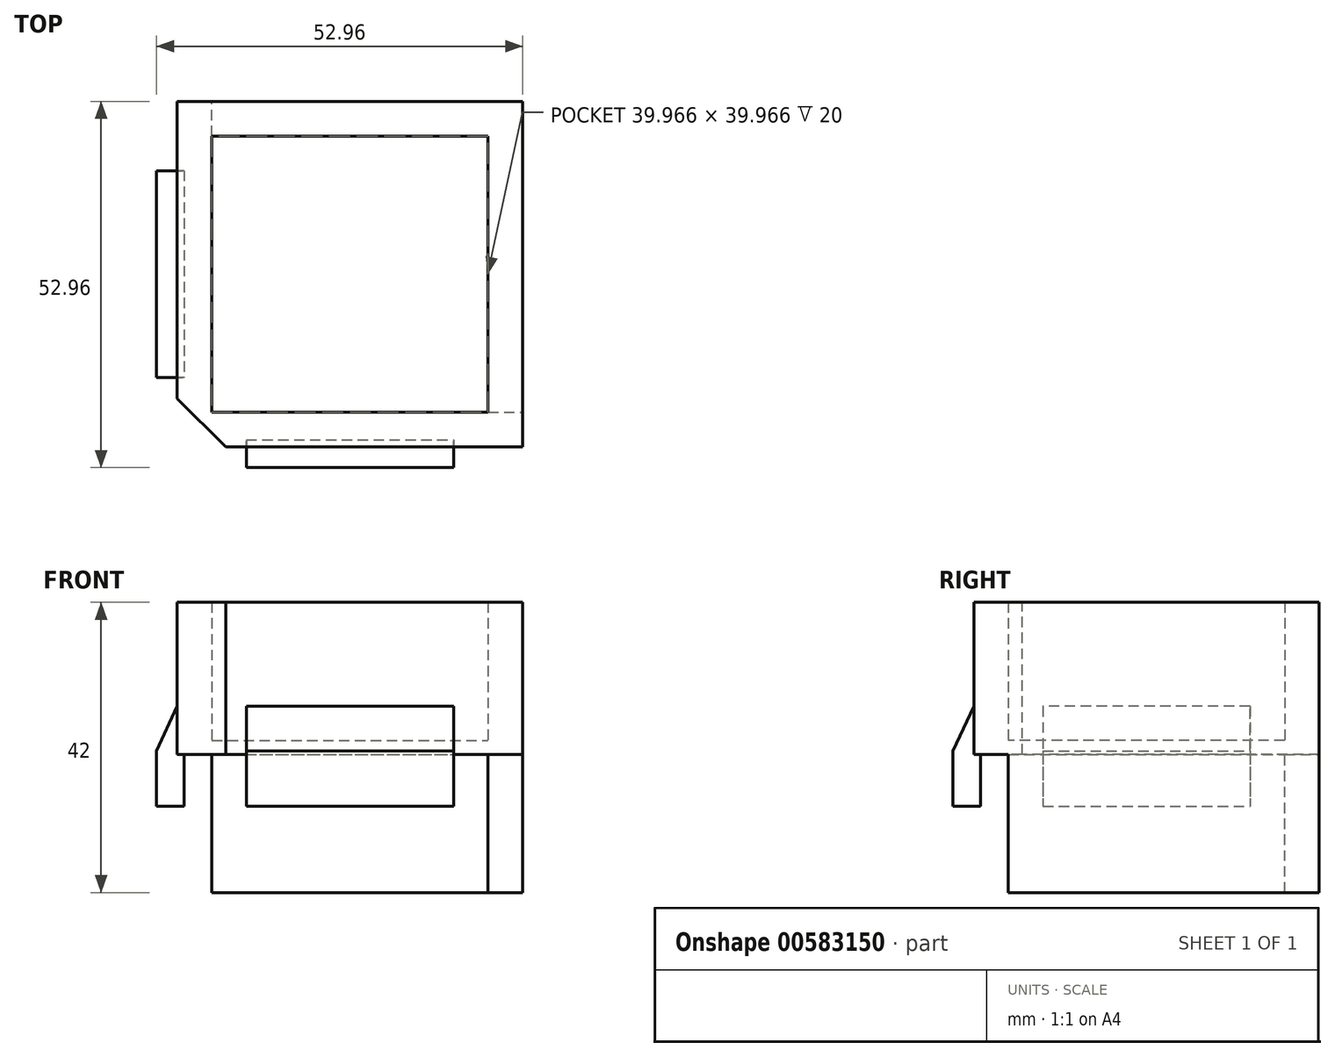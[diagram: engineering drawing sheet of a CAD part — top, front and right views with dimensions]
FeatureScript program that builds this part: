
annotation { "Feature Type Name" : "Feature", "Feature Type Description" : "" }
export const myFeature = defineFeature(function(context is Context, id is Id, definition is map)
    precondition{}
    {
        {
            var Q0;
            Q0=qCreatedBy(makeId("Top.planeOp"),FACE);
            var sketch = newSketch(context, id + "F0", { "sketchPlane" : qUnion([Q0])});
            skLineSegment(sketch, "E0.bottom", {"start": v(-24.98, 24.98) * mm, "end": v(24.98, 24.98) * mm});
            skLineSegment(sketch, "E0.top", {"start": v(-24.98, -24.98) * mm, "end": v(24.98, -24.98) * mm});
            skLineSegment(sketch, "E0.left", {"start": v(-24.98, 24.98) * mm, "end": v(-24.98, -24.98) * mm});
            skLineSegment(sketch, "E0.right", {"start": v(24.98, 24.98) * mm, "end": v(24.98, -24.98) * mm});
            skPoint(sketch, "E0.middle", {"position": v(0, 0) * mm});
            skLineSegment(sketch, "E1.0", {"start": v(-19.98, 19.98) * mm, "end": v(19.98, 19.98) * mm});
            skLineSegment(sketch, "E1.1", {"start": v(-19.98, 19.98) * mm, "end": v(-19.98, -19.98) * mm});
            skLineSegment(sketch, "E1.2", {"start": v(-19.98, -19.98) * mm, "end": v(19.98, -19.98) * mm});
            skLineSegment(sketch, "E1.3", {"start": v(19.98, 19.98) * mm, "end": v(19.98, -19.98) * mm});
            skLineSegment(sketch, "E2", {"start": v(-19.98, -19.98) * mm, "end": v(-19.98, -24.98) * mm});
            skLineSegment(sketch, "E3", {"start": v(19.98, 19.98) * mm, "end": v(24.98, 19.98) * mm});
            skSolve(sketch);
        }
        {
            var Q0;
            Q0=makeQuery(id+"F0.imprint","IMPRINT",FACE,{"disambiguationData":[TD([[makeQuery(id+"F0.imprint","IMPRINT",EDGE,{"derivedFrom":sQuery(id+"F0.wireOp",EDGE,"E1.2")}),-1.0]])]});
            var Q1;
            {var subQ1=sQuery(id+"F0.wireOp",EDGE,"E0.bottom");Q1=makeQuery(id+"F0.imprint","IMPRINT",FACE,{"disambiguationData":[TD([[makeQuery(id+"F0.imprint","IMPRINT",EDGE,{"derivedFrom":subQ1}),-1.0]])]});}
            extrude(context, id + "F1", {"entities" : qUnion([Q0, Q1]), "depth" : 20 * mm, "offsetDistance" : 25 * mm});
        }
        {
            var Q0;
            {var subQ1=sQuery(id+"F0.wireOp",EDGE,"E0.bottom");Q0=makeQuery(id+"F0.imprint","IMPRINT",FACE,{"disambiguationData":[TD([[makeQuery(id+"F0.imprint","IMPRINT",EDGE,{"derivedFrom":subQ1}),-1.0]])]});}
            var Q1;
            Q1=makeQuery(id+"F0.imprint","IMPRINT",FACE,{"disambiguationData":[TD([[makeQuery(id+"F0.imprint","IMPRINT",EDGE,{"derivedFrom":sQuery(id+"F0.wireOp",EDGE,"E1.0")}),-1.0]])]});
            var Q2;
            Q2=makeQuery(id+"F0.imprint","IMPRINT",FACE,{"disambiguationData":[TD([[makeQuery(id+"F0.imprint","IMPRINT",EDGE,{"derivedFrom":sQuery(id+"F0.wireOp",EDGE,"E1.2")}),-1.0]])]});
            extrude(context, id + "F2", {"entities" : qUnion([Q0, Q1, Q2]), "operationType" : NewBodyOperationType.ADD, "oppositeDirection" : true, "depth" : 2 * mm, "offsetDistance" : 25 * mm});
        }
        {
            var Q0;
            Q0=makeQuery(id+"F2.opExtrude","CAP_FACE",FACE,{"disambiguationData":[OSD([sQuery(id+"F0.wireOp",EDGE,"E0.bottom"),sQuery(id+"F0.wireOp",EDGE,"E0.top"),sQuery(id+"F0.wireOp",EDGE,"E0.left"),sQuery(id+"F0.wireOp",EDGE,"E0.right")])],"isStart":false});
            var sketch = newSketch(context, id + "F3", { "sketchPlane" : qUnion([Q0])});
            skLineSegment(sketch, "E4.bottom", {"start": v(-24.98, 24.98) * mm, "end": v(24.98, 24.98) * mm});
            skLineSegment(sketch, "E4.top", {"start": v(-24.98, -24.98) * mm, "end": v(24.98, -24.98) * mm});
            skLineSegment(sketch, "E4.left", {"start": v(-24.98, 24.98) * mm, "end": v(-24.98, -24.98) * mm});
            skLineSegment(sketch, "E4.right", {"start": v(24.98, 24.98) * mm, "end": v(24.98, -24.98) * mm});
            skPoint(sketch, "E4.middle", {"position": v(0, 0) * mm});
            skLineSegment(sketch, "E5.0", {"start": v(-19.98, 19.98) * mm, "end": v(19.98, 19.98) * mm});
            skLineSegment(sketch, "E5.1", {"start": v(-19.98, 19.98) * mm, "end": v(-19.98, -19.98) * mm});
            skLineSegment(sketch, "E5.2", {"start": v(-19.98, -19.98) * mm, "end": v(19.98, -19.98) * mm});
            skLineSegment(sketch, "E5.3", {"start": v(19.98, 19.98) * mm, "end": v(19.98, -19.98) * mm});
            skLineSegment(sketch, "E6", {"start": v(-19.98, -19.98) * mm, "end": v(-19.98, -24.98) * mm});
            skLineSegment(sketch, "E7", {"start": v(19.98, 19.98) * mm, "end": v(24.98, 19.98) * mm});
            skSolve(sketch);
        }
        {
            var Q0;
            Q0=makeQuery(id+"F3.imprint","IMPRINT",FACE,{"disambiguationData":[TD([[makeQuery(id+"F3.imprint","IMPRINT",EDGE,{"derivedFrom":sQuery(id+"F3.wireOp",EDGE,"E5.2")}),-1.0]])]});
            extrude(context, id + "F4", {"entities" : qUnion([Q0]), "operationType" : NewBodyOperationType.ADD, "depth" : 20 * mm, "offsetDistance" : 25 * mm});
        }
        {
            var Q0;
            {var subQ0=sQuery(id+"F0.wireOp",EDGE,"E0.left");Q0=makeQuery(id+"F2.boolean.opBoolean","MERGE",FACE,{"derivedFrom":[makeQuery(id+"F1.opExtrude","SWEPT_FACE",FACE,{"disambiguationData":[OSD([subQ0])]}),makeQuery(id+"F2.opExtrude","SWEPT_FACE",FACE,{"disambiguationData":[OSD([subQ0])]})]});}
            var sketch = newSketch(context, id + "F5", { "sketchPlane" : qUnion([Q0])});
            skLineSegment(sketch, "E8.bottom", {"start": v(14.98, 5.5) * mm, "end": v(-14.98, 5.5) * mm});
            skLineSegment(sketch, "E8.top", {"start": v(14.98, -9.5) * mm, "end": v(-14.98, -9.5) * mm});
            skLineSegment(sketch, "E8.left", {"start": v(14.98, 5.5) * mm, "end": v(14.98, -9.5) * mm});
            skLineSegment(sketch, "E8.right", {"start": v(-14.98, 5.5) * mm, "end": v(-14.98, -9.5) * mm});
            skPoint(sketch, "E8.middle", {"position": v(0, -2) * mm});
            skSolve(sketch);
        }
        {
            var Q0;
            {var subQ0=sQuery(id+"F5.wireOp",EDGE,"E8.bottom");Q0=makeQuery(id+"F5.imprint","IMPRINT",FACE,{"disambiguationData":[TD([[makeQuery(id+"F5.imprint","IMPRINT",EDGE,{"derivedFrom":subQ0}),1.0]])]});}
            var Q1;
            {var subQ0=sQuery(id+"F5.wireOp",EDGE,"E8.top");Q1=makeQuery(id+"F5.imprint","IMPRINT",FACE,{"disambiguationData":[TD([[makeQuery(id+"F5.imprint","IMPRINT",EDGE,{"derivedFrom":subQ0}),-1.0]])]});}
            extrude(context, id + "F6", {"entities" : qUnion([Q0, Q1]), "operationType" : NewBodyOperationType.ADD, "depth" : 3 * mm, "offsetDistance" : 25 * mm});
        }
        {
            var Q0;
            Q0=makeQuery(id+"F6.opExtrude","CAP_EDGE",EDGE,{"disambiguationData":[OSD([sQuery(id+"F5.wireOp",EDGE,"E8.bottom")])],"isStart":false});
            chamfer(context, id + "F7", {"entities" : qUnion([Q0]), "chamferType" : ChamferType.OFFSET_ANGLE, "width" : 7 * mm, "oppositeDirection" : false, "angle" : 25 * degree, "tangentPropagation" : true});
        }
        {
            var Q0;
            {var subQ0=sQuery(id+"F0.wireOp",EDGE,"E0.top");Q0=makeQuery(id+"F2.boolean.opBoolean","MERGE",FACE,{"derivedFrom":[makeQuery(id+"F1.opExtrude","SWEPT_FACE",FACE,{"disambiguationData":[OSD([subQ0])]}),makeQuery(id+"F2.opExtrude","SWEPT_FACE",FACE,{"disambiguationData":[OSD([subQ0])]})]});}
            var sketch = newSketch(context, id + "F8", { "sketchPlane" : qUnion([Q0])});
            skLineSegment(sketch, "E9.bottom", {"start": v(14.98, 5.5) * mm, "end": v(-14.98, 5.5) * mm});
            skLineSegment(sketch, "E9.top", {"start": v(14.98, -9.5) * mm, "end": v(-14.98, -9.5) * mm});
            skLineSegment(sketch, "E9.left", {"start": v(14.98, 5.5) * mm, "end": v(14.98, -9.5) * mm});
            skLineSegment(sketch, "E9.right", {"start": v(-14.98, 5.5) * mm, "end": v(-14.98, -9.5) * mm});
            skPoint(sketch, "E9.middle", {"position": v(0, -2) * mm});
            skSolve(sketch);
        }
        {
            var Q0;
            {var subQ0=sQuery(id+"F8.wireOp",EDGE,"E9.bottom");Q0=makeQuery(id+"F8.imprint","IMPRINT",FACE,{"disambiguationData":[TD([[makeQuery(id+"F8.imprint","IMPRINT",EDGE,{"derivedFrom":subQ0}),1.0]])]});}
            var Q1;
            {var subQ0=sQuery(id+"F8.wireOp",EDGE,"E9.top");Q1=makeQuery(id+"F8.imprint","IMPRINT",FACE,{"disambiguationData":[TD([[makeQuery(id+"F8.imprint","IMPRINT",EDGE,{"derivedFrom":subQ0}),-1.0]])]});}
            extrude(context, id + "F9", {"entities" : qUnion([Q0, Q1]), "operationType" : NewBodyOperationType.ADD, "depth" : 3 * mm, "offsetDistance" : 25 * mm});
        }
        {
            var Q0;
            Q0=makeQuery(id+"F9.opExtrude","CAP_EDGE",EDGE,{"disambiguationData":[OSD([sQuery(id+"F8.wireOp",EDGE,"E9.bottom")])],"isStart":false});
            chamfer(context, id + "F10", {"entities" : qUnion([Q0]), "chamferType" : ChamferType.OFFSET_ANGLE, "width" : 7 * mm, "oppositeDirection" : false, "angle" : 25 * degree, "tangentPropagation" : true});
        }
        {
            var Q0;
            Q0=makeQuery(id+"F9.opExtrude","CAP_FACE",FACE,{"disambiguationData":[OSD([sQuery(id+"F8.wireOp",EDGE,"E9.bottom"),sQuery(id+"F8.wireOp",EDGE,"E9.top"),sQuery(id+"F8.wireOp",EDGE,"E9.left"),sQuery(id+"F8.wireOp",EDGE,"E9.right")])],"isStart":true});
            extrude(context, id + "F11", {"entities" : qUnion([Q0]), "operationType" : NewBodyOperationType.ADD, "depth" : 1 * mm, "offsetDistance" : 25 * mm});
        }
        {
            var Q0;
            Q0=makeQuery(id+"F6.opExtrude","CAP_FACE",FACE,{"disambiguationData":[OSD([sQuery(id+"F5.wireOp",EDGE,"E8.bottom"),sQuery(id+"F5.wireOp",EDGE,"E8.top"),sQuery(id+"F5.wireOp",EDGE,"E8.left"),sQuery(id+"F5.wireOp",EDGE,"E8.right")])],"isStart":true});
            extrude(context, id + "F12", {"entities" : qUnion([Q0]), "operationType" : NewBodyOperationType.ADD, "depth" : 1 * mm, "offsetDistance" : 25 * mm});
        }
        {
            var Q0;
            {var subQ0=sQuery(id+"F0.wireOp",EDGE,"E0.left");var subQ1=sQuery(id+"F0.wireOp",EDGE,"E0.top");Q0=makeQuery(id+"F2.boolean.opBoolean","MERGE",EDGE,{"derivedFrom":[makeQuery(id+"F1.opExtrude","SWEPT_EDGE",EDGE,{"disambiguationData":[OSD([subQ1,subQ0])]}),makeQuery(id+"F2.opExtrude","SWEPT_EDGE",EDGE,{"disambiguationData":[OSD([subQ1,subQ0])]})]});}
            chamfer(context, id + "F13", {"entities" : qUnion([Q0]), "width" : 7 * mm, "tangentPropagation" : true});
        }
    });
